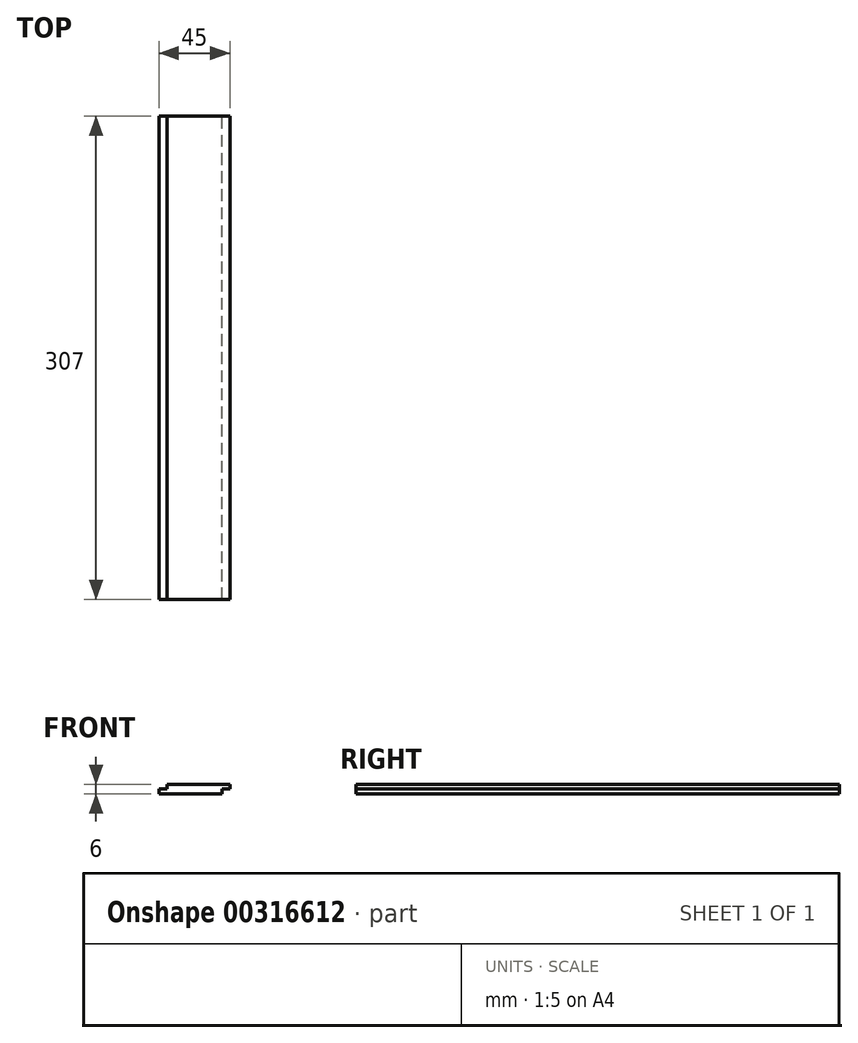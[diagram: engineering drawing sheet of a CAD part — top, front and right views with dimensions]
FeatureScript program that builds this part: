
annotation { "Feature Type Name" : "Feature", "Feature Type Description" : "" }
export const myFeature = defineFeature(function(context is Context, id is Id, definition is map)
    precondition{}
    {
        {
            var Q0;
            Q0=qCreatedBy(makeId("Front.planeOp"),FACE);
            var sketch = newSketch(context, id + "F0", { "sketchPlane" : qUnion([Q0])});
            skLineSegment(sketch, "E0", {"start": v(0, 0) * mm, "end": v(5, 0) * mm});
            skLineSegment(sketch, "E1", {"start": v(5, 0) * mm, "end": v(5, 3) * mm});
            skLineSegment(sketch, "E2", {"start": v(5, 3) * mm, "end": v(45, 3) * mm});
            skLineSegment(sketch, "E3", {"start": v(45, 3) * mm, "end": v(45, 0) * mm});
            skLineSegment(sketch, "E4", {"start": v(45, 0) * mm, "end": v(40, 0) * mm});
            skLineSegment(sketch, "E5", {"start": v(40, 0) * mm, "end": v(40, -3) * mm});
            skLineSegment(sketch, "E6", {"start": v(40, -3) * mm, "end": v(0, -3) * mm});
            skLineSegment(sketch, "E7", {"start": v(0, -3) * mm, "end": v(0, 0) * mm});
            skSolve(sketch);
        }
        {
            var Q0;
            Q0=makeQuery(id+"F0.imprint","IMPRINT",FACE,{"disambiguationData":[TD([[makeQuery(id+"F0.imprint","IMPRINT",EDGE,{"derivedFrom":sQuery(id+"F0.wireOp",EDGE,"E0")}),-1.0]])]});
            extrude(context, id + "F1", {"entities" : qUnion([Q0]), "depth" : 307 * mm});
        }
    });
